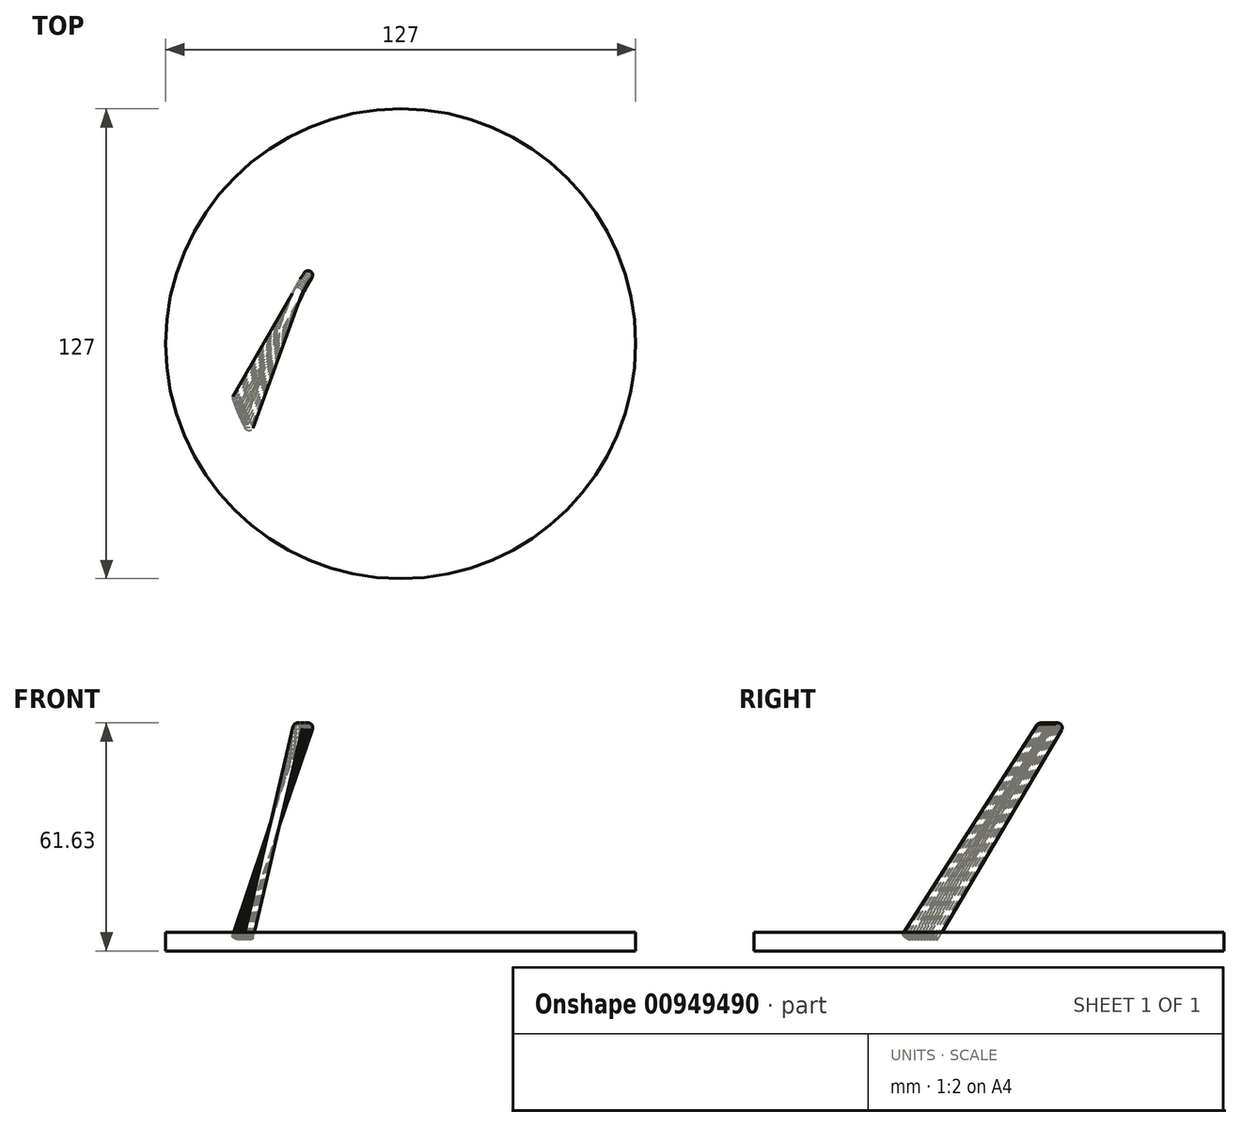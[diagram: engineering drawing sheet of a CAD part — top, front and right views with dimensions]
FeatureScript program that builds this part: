
annotation { "Feature Type Name" : "Feature", "Feature Type Description" : "" }
export const myFeature = defineFeature(function(context is Context, id is Id, definition is map)
    precondition{}
    {
        {
            var Q0;
            Q0=qCreatedBy(makeId("Top.planeOp"),FACE);
            var sketch = newSketch(context, id + "F0", { "sketchPlane" : qUnion([Q0])});
            skCircle(sketch, "E0", {"center": v(0, 0) * mm, "radius": 63.5 * mm});
            skCircle(sketch, "E1", {"center": v(0, 0) * mm, "radius": 12.7 * mm});
            skSolve(sketch);
        }
        {
            var Q0;
            Q0=makeQuery(id+"F0.imprint","IMPRINT",FACE,{"disambiguationData":[TD([[makeQuery(id+"F0.imprint","IMPRINT",EDGE,{"derivedFrom":sQuery(id+"F0.wireOp",EDGE,"E0")}),1.0]])]});
            var Q1;
            Q1=makeQuery(id+"F0.imprint","IMPRINT",FACE,{"disambiguationData":[TD([[makeQuery(id+"F0.imprint","IMPRINT",EDGE,{"derivedFrom":sQuery(id+"F0.wireOp",EDGE,"E1")}),1.0]])]});
            extrude(context, id + "F1", {"entities" : qUnion([Q0, Q1]), "depth" : 5.08 * mm, "offsetDistance" : 25.4 * mm});
        }
        {
            var Q0;
            Q0=qCreatedBy(makeId("Front.planeOp"),FACE);
            var sketch = newSketch(context, id + "F2", { "sketchPlane" : qUnion([Q0])});
            skLineSegment(sketch, "E2", {"start": v(-57.75, 4.42) * mm, "end": v(-19.12, 61.09) * mm});
            skLineSegment(sketch, "E3", {"start": v(-57.75, 4.42) * mm, "end": v(-55.71, 3.03) * mm});
            skLineSegment(sketch, "E4", {"start": v(-55.71, 3.03) * mm, "end": v(-17.08, 59.7) * mm});
            skLineSegment(sketch, "E5", {"start": v(-17.08, 59.7) * mm, "end": v(-19.12, 61.09) * mm});
            skArc(sketch, "E6", {"start": v(-17.08, 59.7) * mm, "mid": v(-17.4, 61.41) * mm, "end": v(-19.12, 61.09) * mm});
            skLineSegment(sketch, "E7", {"start": v(-17.4, 61.41) * mm, "end": v(-56.73, 3.73) * mm});
            skSolve(sketch);
        }
        {
            var Q0;
            {var subQ0=sQuery(id+"F2.wireOp",EDGE,"E2");Q0=makeQuery(id+"F2.imprint","IMPRINT",FACE,{"disambiguationData":[TD([[makeQuery(id+"F2.imprint","IMPRINT",EDGE,{"derivedFrom":subQ0}),-1.0]])]});}
            var Q1;
            {var subQ0=sQuery(id+"F2.wireOp",EDGE,"E6");var subQ3=sQuery(id+"F2.wireOp",EDGE,"E7");var subQ5=makeQuery(id+"F2.imprint","INTERSECT",VERTEX,{"derivedFrom":[subQ0,subQ3]});Q1=makeQuery(id+"F2.imprint","IMPRINT",FACE,{"disambiguationData":[TD([[makeQuery(id+"F2.imprint","IMPRINT",EDGE,{"disambiguationData":[TD([[subQ5,-1.0]])],"derivedFrom":subQ3}),-1.0]])]});}
            var Q2;
            Q2=sQuery(id+"F2.wireOp",EDGE,"E7");
            revolve(context, id + "F3", {"surfaceOperationType" : NewSurfaceOperationType.NEW, "entities" : qUnion([Q0, Q1]), "axis" : qUnion([Q2]), "revolveType" : RevolveType.FULL});
        }
        {
            var Q0;
            Q0=qCreatedBy(makeId("Front.planeOp"),FACE);
            var sketch = newSketch(context, id + "F4", { "sketchPlane" : qUnion([Q0])});
            skLineSegment(sketch, "E8", {"start": v(-32.9, 5.62) * mm, "end": v(-32.9, 54.66) * mm});
            skSolve(sketch);
        }
        {
            var Q0;
            Q0=makeQuery(id+"F3.opRevolve","SWEPT_BODY",BODY,{"disambiguationData":[OSD([sQuery(id+"F2.wireOp",EDGE,"E2"),sQuery(id+"F2.wireOp",EDGE,"E3"),sQuery(id+"F2.wireOp",EDGE,"E6"),sQuery(id+"F2.wireOp",EDGE,"E7")])]});
            var Q1;
            Q1=sQuery(id+"F4.wireOp",EDGE,"E8");
            transform(context, id + "F5", {"entities" : qUnion([Q0]), "transformType" : TransformType.ROTATION, "transformAxis" : qUnion([Q1]), "angle" : 70 * degree, "makeCopy" : false});
        }
        {
            var Q0;
            Q0=qCreatedBy(makeId("Front.planeOp"),FACE);
            var sketch = newSketch(context, id + "F6", { "sketchPlane" : qUnion([Q0])});
            skLineSegment(sketch, "E9", {"start": v(0, 0) * mm, "end": v(0, 67.38) * mm});
            skLineSegment(sketch, "E10", {"start": v(0, 67.38) * mm, "end": v(0, 0) * mm});
            skSolve(sketch);
        }
        {
            var Q0;
            Q0=makeQuery(id+"F3.opRevolve","SWEPT_BODY",BODY,{"disambiguationData":[OSD([sQuery(id+"F2.wireOp",EDGE,"E2"),sQuery(id+"F2.wireOp",EDGE,"E3"),sQuery(id+"F2.wireOp",EDGE,"E6"),sQuery(id+"F2.wireOp",EDGE,"E7")])]});
            var Q1;
            Q1=sQuery(id+"F6.wireOp",EDGE,"E10");
            circularPattern(context, id + "F7", {"entities" : qUnion([Q0]), "axis" : qUnion([Q1]), "angle" : 10 * degree, "instanceCount" : 10, "equalSpace" : true});
        }
    });
